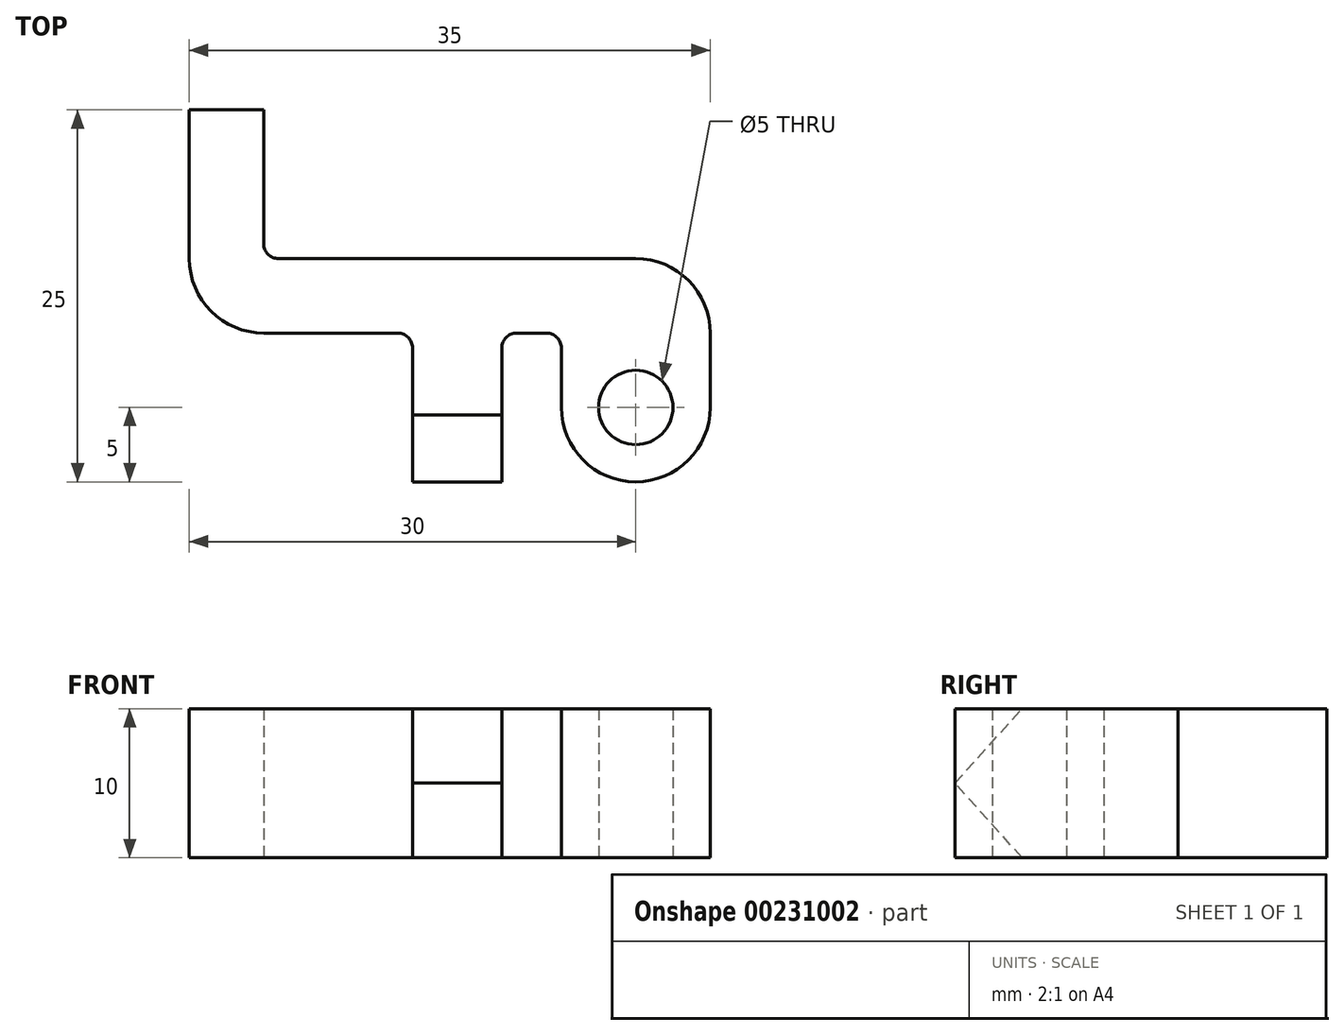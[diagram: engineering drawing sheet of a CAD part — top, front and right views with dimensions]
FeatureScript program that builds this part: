
annotation { "Feature Type Name" : "Feature", "Feature Type Description" : "" }
export const myFeature = defineFeature(function(context is Context, id is Id, definition is map)
    precondition{}
    {
        {
            var Q0;
            Q0=qCreatedBy(makeId("Top.planeOp"),FACE);
            var sketch = newSketch(context, id + "F0", { "sketchPlane" : qUnion([Q0])});
            skLineSegment(sketch, "E0", {"start": v(0, 0) * mm, "end": v(0, 25) * mm});
            skLineSegment(sketch, "E1", {"start": v(0, 25) * mm, "end": v(5, 25) * mm});
            skLineSegment(sketch, "E2", {"start": v(5, 25) * mm, "end": v(5, 15) * mm});
            skLineSegment(sketch, "E3", {"start": v(5, 15) * mm, "end": v(35, 15) * mm});
            skLineSegment(sketch, "E4", {"start": v(35, 15) * mm, "end": v(35, 5) * mm});
            skLineSegment(sketch, "E5", {"start": v(25, 5) * mm, "end": v(25, 10) * mm});
            skLineSegment(sketch, "E6", {"start": v(25, 10) * mm, "end": v(21, 10) * mm});
            skLineSegment(sketch, "E7", {"start": v(21, 10) * mm, "end": v(21, 0) * mm});
            skLineSegment(sketch, "E8", {"start": v(21, 0) * mm, "end": v(15, 0) * mm});
            skLineSegment(sketch, "E9", {"start": v(15, 0) * mm, "end": v(15, 10) * mm});
            skLineSegment(sketch, "E10", {"start": v(15, 10) * mm, "end": v(0, 10) * mm});
            skCircle(sketch, "E11", {"center": v(30, 5) * mm, "radius": 2.5 * mm});
            skArc(sketch, "E12", {"start": v(25, 5) * mm, "mid": v(30, 0) * mm, "end": v(35, 5) * mm});
            skPoint(sketch, "E13.orphan", {"position": v(25, 0) * mm});
            skPoint(sketch, "E14.start.orphan", {"position": v(35, 0) * mm});
            skSolve(sketch);
        }
        {
            var Q0;
            {var subQ0=sQuery(id+"F0.wireOp",EDGE,"E1");Q0=makeQuery(id+"F0.imprint","IMPRINT",FACE,{"disambiguationData":[TD([[makeQuery(id+"F0.imprint","IMPRINT",EDGE,{"derivedFrom":subQ0}),-1.0]])]});}
            extrude(context, id + "F1", {"entities" : qUnion([Q0]), "depth" : 10 * mm});
        }
        {
            var Q0;
            Q0=makeQuery(id+"F1.opExtrude","SWEPT_EDGE",EDGE,{"disambiguationData":[OSD([sQuery(id+"F0.wireOp",EDGE,"E0"),sQuery(id+"F0.wireOp",EDGE,"E10")])]});
            var Q1;
            Q1=makeQuery(id+"F1.opExtrude","SWEPT_EDGE",EDGE,{"disambiguationData":[OSD([sQuery(id+"F0.wireOp",EDGE,"E3"),sQuery(id+"F0.wireOp",EDGE,"E4")])]});
            fillet(context, id + "F2", {"entities" : qUnion([Q0, Q1]), "radius" : 5 * mm, "tangentPropagation" : true, "allowEdgeOverflow" : false});
        }
        {
            var Q0;
            Q0=makeQuery(id+"F1.opExtrude","SWEPT_EDGE",EDGE,{"disambiguationData":[OSD([sQuery(id+"F0.wireOp",EDGE,"E9"),sQuery(id+"F0.wireOp",EDGE,"E10")])]});
            var Q1;
            Q1=makeQuery(id+"F1.opExtrude","SWEPT_EDGE",EDGE,{"disambiguationData":[OSD([sQuery(id+"F0.wireOp",EDGE,"E2"),sQuery(id+"F0.wireOp",EDGE,"E3")])]});
            var Q2;
            Q2=makeQuery(id+"F1.opExtrude","SWEPT_EDGE",EDGE,{"disambiguationData":[OSD([sQuery(id+"F0.wireOp",EDGE,"E5"),sQuery(id+"F0.wireOp",EDGE,"E6")])]});
            var Q3;
            Q3=makeQuery(id+"F1.opExtrude","SWEPT_EDGE",EDGE,{"disambiguationData":[OSD([sQuery(id+"F0.wireOp",EDGE,"E6"),sQuery(id+"F0.wireOp",EDGE,"E7")])]});
            fillet(context, id + "F3", {"entities" : qUnion([Q0, Q1, Q2, Q3]), "radius" : 1 * mm, "tangentPropagation" : true, "allowEdgeOverflow" : false});
        }
        {
            var Q0;
            Q0=makeQuery(id+"F1.opExtrude","SWEPT_FACE",FACE,{"disambiguationData":[OSD([sQuery(id+"F0.wireOp",EDGE,"E9")])]});
            var sketch = newSketch(context, id + "F4", { "sketchPlane" : qUnion([Q0])});
            skLineSegment(sketch, "E15", {"start": v(-4.5, 0) * mm, "end": v(0, 5) * mm});
            skLineSegment(sketch, "E16", {"start": v(0, 5) * mm, "end": v(-4.5, 10) * mm});
            skLineSegment(sketch, "E17", {"start": v(-4.5, 10) * mm, "end": v(0, 10) * mm});
            skLineSegment(sketch, "E18", {"start": v(0, 10) * mm, "end": v(0, 0) * mm});
            skLineSegment(sketch, "E19", {"start": v(0, 0) * mm, "end": v(-4.5, 0) * mm});
            skSolve(sketch);
        }
        {
            var Q0;
            {var subQ0=sQuery(id+"F4.wireOp",EDGE,"E16");Q0=makeQuery(id+"F4.imprint","IMPRINT",FACE,{"disambiguationData":[TD([[makeQuery(id+"F4.imprint","IMPRINT",EDGE,{"derivedFrom":subQ0}),-1.0]])]});}
            var Q1;
            {var subQ0=sQuery(id+"F4.wireOp",EDGE,"E15");Q1=makeQuery(id+"F4.imprint","IMPRINT",FACE,{"disambiguationData":[TD([[makeQuery(id+"F4.imprint","IMPRINT",EDGE,{"derivedFrom":subQ0}),-1.0]])]});}
            extrude(context, id + "F5", {"entities" : qUnion([Q0, Q1]), "operationType" : NewBodyOperationType.REMOVE, "oppositeDirection" : true, "depth" : 6 * mm});
        }
    });
